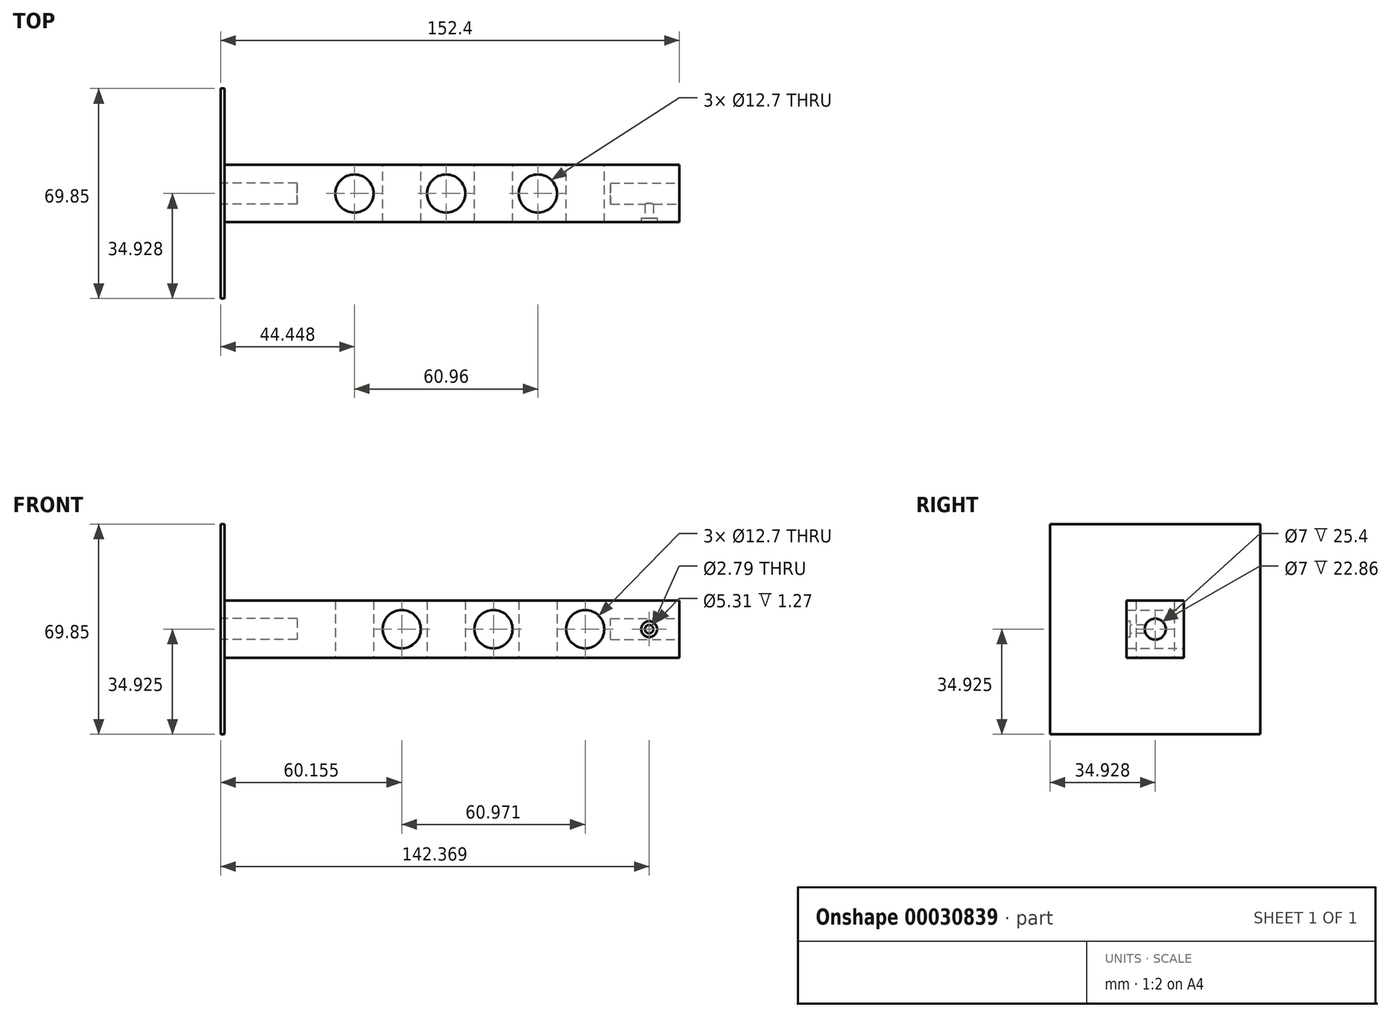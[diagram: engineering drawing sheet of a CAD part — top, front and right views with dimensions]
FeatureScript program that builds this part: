
annotation { "Feature Type Name" : "Feature", "Feature Type Description" : "" }
export const myFeature = defineFeature(function(context is Context, id is Id, definition is map)
    precondition{}
    {
        {
            var Q0;
            Q0=qCreatedBy(makeId("Top.planeOp"),FACE);
            var sketch = newSketch(context, id + "F0", { "sketchPlane" : qUnion([Q0])});
            skLineSegment(sketch, "E0.bottom", {"start": v(-82.05, -1.77) * mm, "end": v(70.35, -1.77) * mm});
            skLineSegment(sketch, "E0.top", {"start": v(-82.05, 17.28) * mm, "end": v(70.35, 17.28) * mm});
            skLineSegment(sketch, "E0.left", {"start": v(-82.05, -1.77) * mm, "end": v(-82.05, 17.28) * mm});
            skLineSegment(sketch, "E0.right", {"start": v(70.35, -1.77) * mm, "end": v(70.35, 17.28) * mm});
            skPoint(sketch, "E1", {"position": v(-56.65, 17.28) * mm});
            skCircle(sketch, "E2", {"center": v(-37.6, 7.76) * mm, "radius": 6.35 * mm});
            skPoint(sketch, "E3", {"position": v(-7.12, 7.76) * mm});
            skCircle(sketch, "E4", {"center": v(-7.12, 7.76) * mm, "radius": 6.35 * mm});
            skPoint(sketch, "E5", {"position": v(23.36, 7.76) * mm});
            skCircle(sketch, "E6", {"center": v(23.36, 7.76) * mm, "radius": 6.35 * mm});
            skPoint(sketch, "E7.orphan", {"position": v(-82.05, 7.76) * mm});
            skPoint(sketch, "E8.end.orphan", {"position": v(70.35, 7.76) * mm});
            skPoint(sketch, "E9.end.orphan", {"position": v(-56.65, 7.76) * mm});
            skPoint(sketch, "E10", {"position": v(-22.36, 7.76) * mm});
            skSolve(sketch);
        }
        {
            var Q0;
            Q0 = qSketchRegion(id + "F0", true);
            extrude(context, id + "F1", {"entities" : qUnion([Q0]), "depth" : 19.05 * mm});
        }
        {
            var Q0;
            Q0=makeQuery(id+"F1.opExtrude","SWEPT_FACE",FACE,{"disambiguationData":[OSD([sQuery(id+"F0.wireOp",EDGE,"E0.top")])]});
            var sketch = newSketch(context, id + "F2", { "sketchPlane" : qUnion([Q0])});
            skPoint(sketch, "E11", {"position": v(21.9, 9.53) * mm});
            skCircle(sketch, "E12", {"center": v(21.9, 9.53) * mm, "radius": 6.35 * mm});
            skPoint(sketch, "E13", {"position": v(-39.08, 9.52) * mm});
            skCircle(sketch, "E14", {"center": v(-39.08, 9.53) * mm, "radius": 6.35 * mm});
            skCircle(sketch, "E15", {"center": v(-8.6, 9.52) * mm, "radius": 6.35 * mm});
            skSolve(sketch);
        }
        {
            var Q0;
            Q0 = qSketchRegion(id + "F2", true);
            extrude(context, id + "F3", {"entities" : qUnion([Q0]), "operationType" : NewBodyOperationType.REMOVE, "oppositeDirection" : true, "depth" : 25.4 * mm});
        }
        {
            var Q0;
            Q0=makeQuery(id+"F1.opExtrude","SWEPT_FACE",FACE,{"disambiguationData":[OSD([sQuery(id+"F0.wireOp",EDGE,"E0.left")])]});
            var sketch = newSketch(context, id + "F4", { "sketchPlane" : qUnion([Q0])});
            skPoint(sketch, "E16.orphan", {"position": v(-7.76, 19.05) * mm});
            skPoint(sketch, "E17.end.orphan", {"position": v(-7.76, 0) * mm});
            skPoint(sketch, "E18.start.orphan", {"position": v(-17.28, 9.53) * mm});
            skPoint(sketch, "E19.trimOffspring.end.orphan", {"position": v(1.77, 9.53) * mm});
            skCircle(sketch, "E20", {"center": v(-7.76, 9.53) * mm, "radius": 3.5 * mm});
            skSolve(sketch);
        }
        {
            var Q0;
            Q0 = qSketchRegion(id + "F4", true);
            extrude(context, id + "F5", {"entities" : qUnion([Q0]), "operationType" : NewBodyOperationType.REMOVE, "oppositeDirection" : true, "depth" : 25.4 * mm});
        }
        {
            var Q0;
            Q0=makeQuery(id+"F1.opExtrude","SWEPT_FACE",FACE,{"disambiguationData":[OSD([sQuery(id+"F0.wireOp",EDGE,"E0.right")])]});
            var sketch = newSketch(context, id + "F6", { "sketchPlane" : qUnion([Q0])});
            skLineSegment(sketch, "E21", {"start": v(7.76, 10.67) * mm, "end": v(7.76, 9.53) * mm});
            skPoint(sketch, "E22.trimOffspring.end.orphan", {"position": v(17.28, 9.53) * mm});
            skPoint(sketch, "E23.orphan", {"position": v(7.76, 0) * mm});
            skPoint(sketch, "E24.start.orphan", {"position": v(-1.77, 9.53) * mm});
            skPoint(sketch, "E25.orphan", {"position": v(7.76, 19.05) * mm});
            skCircle(sketch, "E26", {"center": v(7.76, 9.53) * mm, "radius": 3.5 * mm});
            skSolve(sketch);
        }
        {
            var Q0;
            Q0=makeQuery(id+"F6.imprint","IMPRINT",FACE,{"disambiguationData":[TD([[makeQuery(id+"F6.imprint","IMPRINT",EDGE,{"derivedFrom":sQuery(id+"F6.wireOp",EDGE,"E26")}),1.0]])]});
            extrude(context, id + "F7", {"entities" : qUnion([Q0]), "operationType" : NewBodyOperationType.REMOVE, "oppositeDirection" : true, "depth" : 22.86 * mm});
        }
        {
            var Q0;
            Q0=makeQuery(id+"F1.opExtrude","CAP_FACE",FACE,{"disambiguationData":[OSD([sQuery(id+"F0.wireOp",EDGE,"E0.bottom"),sQuery(id+"F0.wireOp",EDGE,"E0.top"),sQuery(id+"F0.wireOp",EDGE,"E0.left"),sQuery(id+"F0.wireOp",EDGE,"E0.right"),sQuery(id+"F0.wireOp",EDGE,"E2"),sQuery(id+"F0.wireOp",EDGE,"E4"),sQuery(id+"F0.wireOp",EDGE,"E6")])],"isStart":false});
            var sketch = newSketch(context, id + "F8", { "sketchPlane" : qUnion([Q0])});
            skLineSegment(sketch, "E27", {"start": v(-80.78, 17.28) * mm, "end": v(-80.78, -1.77) * mm});
            skSolve(sketch);
        }
        {
            var Q0;
            {var subQ1=sQuery(id+"F8.wireOp",EDGE,"E27");Q0=makeQuery(id+"F8.imprint","IMPRINT",FACE,{"disambiguationData":[TD([[makeQuery(id+"F8.imprint","IMPRINT",EDGE,{"derivedFrom":subQ1}),-1.0]])]});}
            extrude(context, id + "F9", {"entities" : qUnion([Q0]), "operationType" : NewBodyOperationType.ADD, "depth" : 25.4 * mm});
        }
        {
            var Q0;
            {var subQ0=sQuery(id+"F0.wireOp",EDGE,"E0.top");Q0=makeQuery(id+"F9.boolean.opBoolean","MERGE",FACE,{"derivedFrom":[makeQuery(id+"F1.opExtrude","SWEPT_FACE",FACE,{"disambiguationData":[OSD([subQ0])]}),makeQuery(id+"F9.opExtrude","SWEPT_FACE",FACE,{"disambiguationData":[OSD([subQ0])]})]});}
            var sketch = newSketch(context, id + "F10", { "sketchPlane" : qUnion([Q0])});
            skLineSegment(sketch, "E28", {"start": v(80.78, 19.05) * mm, "end": v(80.78, 0) * mm});
            skSolve(sketch);
        }
        {
            var Q0;
            {var subQ2=sQuery(id+"F10.wireOp",EDGE,"E28");Q0=makeQuery(id+"F10.imprint","IMPRINT",FACE,{"disambiguationData":[TD([[makeQuery(id+"F10.imprint","IMPRINT",EDGE,{"derivedFrom":subQ2}),1.0]])]});}
            extrude(context, id + "F11", {"entities" : qUnion([Q0]), "operationType" : NewBodyOperationType.ADD, "depth" : 25.4 * mm});
        }
        {
            var Q0;
            {var subQ0=sQuery(id+"F0.wireOp",EDGE,"E0.bottom");Q0=makeQuery(id+"F9.boolean.opBoolean","MERGE",FACE,{"derivedFrom":[makeQuery(id+"F1.opExtrude","SWEPT_FACE",FACE,{"disambiguationData":[OSD([subQ0])]}),makeQuery(id+"F9.opExtrude","SWEPT_FACE",FACE,{"disambiguationData":[OSD([subQ0])]})]});}
            var sketch = newSketch(context, id + "F12", { "sketchPlane" : qUnion([Q0])});
            skLineSegment(sketch, "E29", {"start": v(-80.78, 19.05) * mm, "end": v(-80.78, 0) * mm});
            skSolve(sketch);
        }
        {
            var Q0;
            {var subQ2=sQuery(id+"F12.wireOp",EDGE,"E29");Q0=makeQuery(id+"F12.imprint","IMPRINT",FACE,{"disambiguationData":[TD([[makeQuery(id+"F12.imprint","IMPRINT",EDGE,{"derivedFrom":subQ2}),-1.0]])]});}
            extrude(context, id + "F13", {"entities" : qUnion([Q0]), "operationType" : NewBodyOperationType.ADD, "depth" : 25.4 * mm});
        }
        {
            var Q0;
            {var subQ0=sQuery(id+"F0.wireOp",EDGE,"E0.bottom");var subQ1=sQuery(id+"F0.wireOp",EDGE,"E0.top");var subQ2=sQuery(id+"F0.wireOp",EDGE,"E0.left");var subQ3=makeQuery(id+"F1.opExtrude","CAP_EDGE",EDGE,{"disambiguationData":[OSD([subQ1])],"isStart":true});var subQ4=makeQuery(id+"F1.opExtrude","CAP_EDGE",EDGE,{"disambiguationData":[OSD([subQ0])],"isStart":true});Q0=makeQuery(id+"F13.boolean.opBoolean","MERGE",FACE,{"derivedFrom":[makeQuery(id+"F11.boolean.opBoolean","MERGE",FACE,{"derivedFrom":[makeQuery(id+"F1.opExtrude","CAP_FACE",FACE,{"disambiguationData":[OSD([subQ0,subQ1,subQ2,sQuery(id+"F0.wireOp",EDGE,"E0.right"),sQuery(id+"F0.wireOp",EDGE,"E2"),sQuery(id+"F0.wireOp",EDGE,"E4"),sQuery(id+"F0.wireOp",EDGE,"E6")])],"isStart":true}),makeQuery(id+"F11.opExtrude","SWEPT_FACE",FACE,{"disambiguationData":[OSD([subQ1]),TDD([makeQuery(id+"F10.imprint","IMPRINT",EDGE,{"disambiguationData":[TD([[makeQuery(id+"F10.imprint","INTERSECT",VERTEX,{"derivedFrom":[subQ3,sQuery(id+"F10.wireOp",EDGE,"E28")]}),1.0]])],"derivedFrom":subQ3})])]})]}),makeQuery(id+"F13.opExtrude","SWEPT_FACE",FACE,{"disambiguationData":[OSD([subQ0]),TDD([makeQuery(id+"F12.imprint","IMPRINT",EDGE,{"disambiguationData":[TD([[makeQuery(id+"F12.imprint","INTERSECT",VERTEX,{"derivedFrom":[subQ4,sQuery(id+"F12.wireOp",EDGE,"E29")]}),1.0]])],"derivedFrom":subQ4})])]})]});}
            var sketch = newSketch(context, id + "F14", { "sketchPlane" : qUnion([Q0])});
            skLineSegment(sketch, "E30", {"start": v(-80.78, 1.77) * mm, "end": v(-80.78, -17.28) * mm});
            skSolve(sketch);
        }
        {
            var Q0;
            Q0=makeQuery(id+"F14.imprint","IMPRINT",FACE,{"disambiguationData":[TD([[makeQuery(id+"F14.imprint","IMPRINT",EDGE,{"derivedFrom":sQuery(id+"F14.wireOp",EDGE,"E30")}),-1.0]])]});
            extrude(context, id + "F15", {"entities" : qUnion([Q0]), "operationType" : NewBodyOperationType.ADD, "depth" : 25.4 * mm});
        }
        {
            var Q0;
            {var subQ0=sQuery(id+"F0.wireOp",EDGE,"E0.bottom");Q0=makeQuery(id+"F9.boolean.opBoolean","MERGE",FACE,{"derivedFrom":[makeQuery(id+"F1.opExtrude","SWEPT_FACE",FACE,{"disambiguationData":[OSD([subQ0])]}),makeQuery(id+"F9.opExtrude","SWEPT_FACE",FACE,{"disambiguationData":[OSD([subQ0])]})]});}
            var sketch = newSketch(context, id + "F16", { "sketchPlane" : qUnion([Q0])});
            skLineSegment(sketch, "E31", {"start": v(70.35, 9.53) * mm, "end": v(46.03, 9.53) * mm});
            skPoint(sketch, "E31.endSnap0", {"position": v(70.35, 9.53) * mm});
            skCircle(sketch, "E32", {"center": v(60.32, 9.53) * mm, "radius": 1.4 * mm});
            skCircle(sketch, "E33", {"center": v(60.32, 9.53) * mm, "radius": 2.65 * mm});
            skSolve(sketch);
        }
        {
            var Q0;
            {var subQ0=sQuery(id+"F16.wireOp",EDGE,"E32");var subQ1=sQuery(id+"F16.wireOp",EDGE,"E31");var subQ3=makeQuery(id+"F16.imprint","INTERSECT",VERTEX,{"disambiguationData":[OD(0.0)],"derivedFrom":[subQ1,subQ0]});Q0=makeQuery(id+"F16.imprint","IMPRINT",FACE,{"disambiguationData":[TD([[makeQuery(id+"F16.imprint","IMPRINT",EDGE,{"disambiguationData":[TD([[subQ3,-1.0]])],"derivedFrom":subQ1}),-1.0]])]});}
            var Q1;
            {var subQ0=sQuery(id+"F16.wireOp",EDGE,"E32");var subQ1=sQuery(id+"F16.wireOp",EDGE,"E31");var subQ3=makeQuery(id+"F16.imprint","INTERSECT",VERTEX,{"disambiguationData":[OD(0.0)],"derivedFrom":[subQ1,subQ0]});Q1=makeQuery(id+"F16.imprint","IMPRINT",FACE,{"disambiguationData":[TD([[makeQuery(id+"F16.imprint","IMPRINT",EDGE,{"disambiguationData":[TD([[subQ3,-1.0]])],"derivedFrom":subQ1}),1.0]])]});}
            extrude(context, id + "F17", {"entities" : qUnion([Q0, Q1]), "operationType" : NewBodyOperationType.REMOVE, "oppositeDirection" : true, "depth" : 7.62 * mm});
        }
        {
            var Q0;
            Q0 = qSketchRegion(id + "F16", true);
            extrude(context, id + "F18", {"entities" : qUnion([Q0]), "operationType" : NewBodyOperationType.REMOVE, "oppositeDirection" : true, "depth" : 1.27 * mm});
        }
    });
